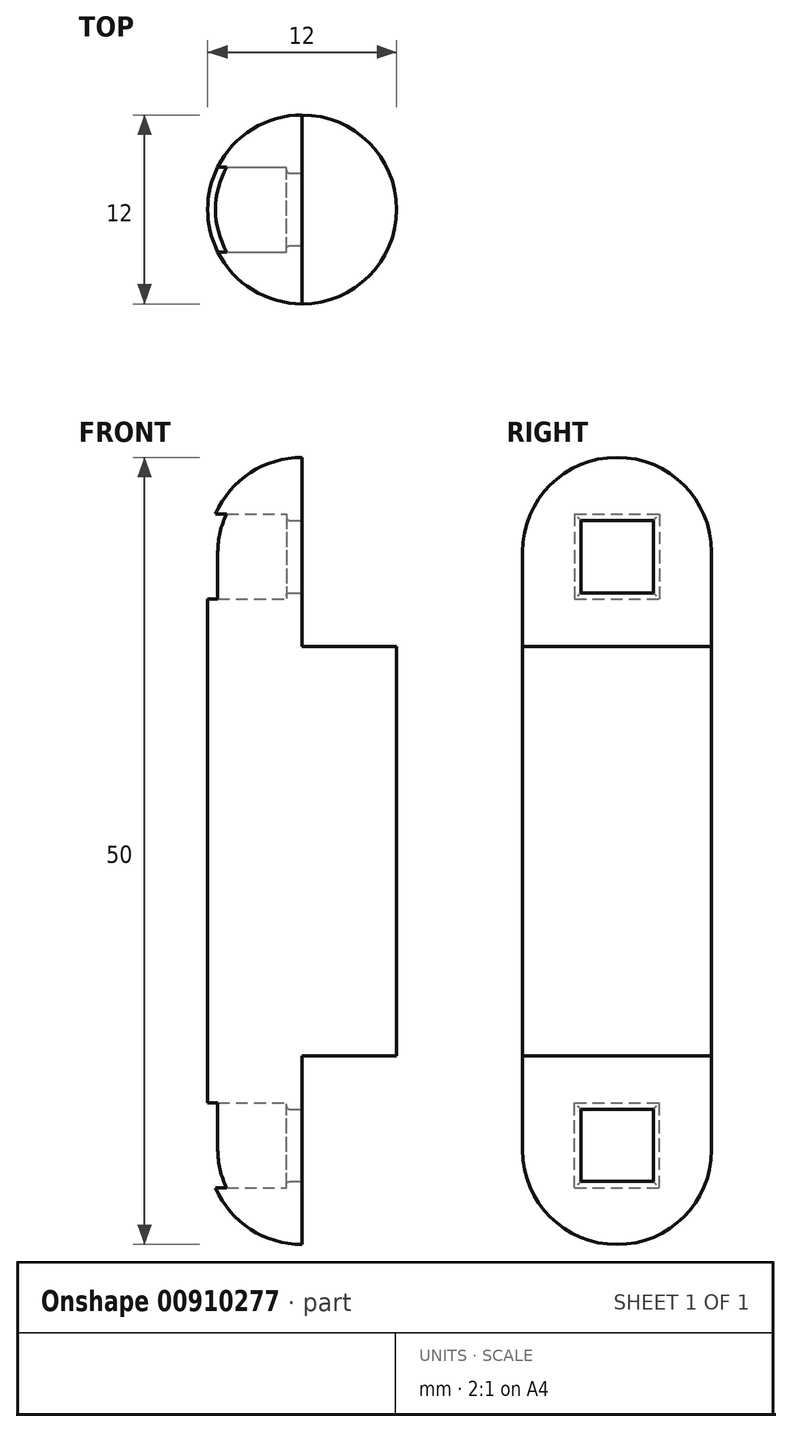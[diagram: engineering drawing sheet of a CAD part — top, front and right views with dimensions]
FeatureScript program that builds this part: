
annotation { "Feature Type Name" : "Feature", "Feature Type Description" : "" }
export const myFeature = defineFeature(function(context is Context, id is Id, definition is map)
    precondition{}
    {
        {
            var Q0;
            Q0=qCreatedBy(makeId("Top.planeOp"),FACE);
            var sketch = newSketch(context, id + "F0", { "sketchPlane" : qUnion([Q0])});
            skCircle(sketch, "E0", {"center": v(0, 0) * mm, "radius": 6 * mm});
            skSolve(sketch);
        }
        {
            var Q0;
            Q0=makeQuery(id+"F0.imprint","IMPRINT",FACE,{"disambiguationData":[TD([[makeQuery(id+"F0.imprint","IMPRINT",EDGE,{"derivedFrom":sQuery(id+"F0.wireOp",EDGE,"E0")}),1.0]])]});
            extrude(context, id + "F1", {"entities" : qUnion([Q0]), "depth" : 25 * mm, "offsetDistance" : 25 * mm});
        }
        {
            var Q0;
            Q0=makeQuery(id+"F1.opExtrude","CAP_EDGE",EDGE,{"disambiguationData":[OSD([sQuery(id+"F0.wireOp",EDGE,"E0")])],"isStart":false});
            fillet(context, id + "F2", {"entities" : qUnion([Q0]), "radius" : 6 * mm, "tangentPropagation" : true, "allowEdgeOverflow" : false});
        }
        {
            var Q0;
            Q0=qCreatedBy(makeId("Front.planeOp"),FACE);
            var sketch = newSketch(context, id + "F3", { "sketchPlane" : qUnion([Q0])});
            skLineSegment(sketch, "E1.bottom", {"start": v(0, 26.9) * mm, "end": v(7.45, 26.9) * mm});
            skLineSegment(sketch, "E1.top", {"start": v(0, 13) * mm, "end": v(7.45, 13) * mm});
            skLineSegment(sketch, "E1.left", {"start": v(0, 26.9) * mm, "end": v(0, 13) * mm});
            skLineSegment(sketch, "E1.right", {"start": v(7.45, 26.9) * mm, "end": v(7.45, 13) * mm});
            skSolve(sketch);
        }
        {
            var Q0;
            Q0=makeQuery(id+"F3.imprint","IMPRINT",FACE,{"disambiguationData":[TD([[makeQuery(id+"F3.imprint","IMPRINT",EDGE,{"derivedFrom":sQuery(id+"F3.wireOp",EDGE,"E1.bottom")}),-1.0]])]});
            extrude(context, id + "F4", {"entities" : qUnion([Q0]), "operationType" : NewBodyOperationType.REMOVE, "endBound" : BoundingType.SYMMETRIC, "depth" : 25 * mm, "offsetDistance" : 25 * mm});
        }
        {
            var Q0;
            Q0=makeQuery(id+"F4.boolean.opBoolean","COPY",FACE,{"derivedFrom":makeQuery(id+"F4.opExtrude","SWEPT_FACE",FACE,{"disambiguationData":[OSD([sQuery(id+"F3.wireOp",EDGE,"E1.left")])]})});
            var sketch = newSketch(context, id + "F5", { "sketchPlane" : qUnion([Q0])});
            skLineSegment(sketch, "E2.bottom", {"start": v(-2.7, 21.4) * mm, "end": v(2.7, 21.4) * mm});
            skLineSegment(sketch, "E2.top", {"start": v(-2.7, 16) * mm, "end": v(2.7, 16) * mm});
            skLineSegment(sketch, "E2.left", {"start": v(-2.7, 21.4) * mm, "end": v(-2.7, 16) * mm});
            skLineSegment(sketch, "E2.right", {"start": v(2.7, 21.4) * mm, "end": v(2.7, 16) * mm});
            skSolve(sketch);
        }
        {
            var Q0;
            Q0=makeQuery(id+"F5.imprint","IMPRINT",FACE,{"disambiguationData":[TD([[makeQuery(id+"F5.imprint","IMPRINT",EDGE,{"derivedFrom":sQuery(id+"F5.wireOp",EDGE,"E2.bottom")}),-1.0]])]});
            extrude(context, id + "F6", {"entities" : qUnion([Q0]), "operationType" : NewBodyOperationType.REMOVE, "oppositeDirection" : true, "depth" : 25 * mm, "offsetDistance" : 25 * mm});
        }
        {
            var Q0;
            Q0=makeQuery(id+"F4.boolean.opBoolean","COPY",FACE,{"derivedFrom":makeQuery(id+"F4.opExtrude","SWEPT_FACE",FACE,{"disambiguationData":[OSD([sQuery(id+"F3.wireOp",EDGE,"E1.left")])]})});
            var sketch = newSketch(context, id + "F7", { "sketchPlane" : qUnion([Q0])});
            skLineSegment(sketch, "E3.bottom", {"start": v(-2.3, 21) * mm, "end": v(2.3, 21) * mm});
            skLineSegment(sketch, "E3.top", {"start": v(-2.3, 16.4) * mm, "end": v(2.3, 16.4) * mm});
            skLineSegment(sketch, "E3.left", {"start": v(-2.3, 21) * mm, "end": v(-2.3, 16.4) * mm});
            skLineSegment(sketch, "E3.right", {"start": v(2.3, 21) * mm, "end": v(2.3, 16.4) * mm});
            skLineSegment(sketch, "E4.bottom", {"start": v(-3.32, 22.07) * mm, "end": v(3.51, 22.07) * mm});
            skLineSegment(sketch, "E4.top", {"start": v(-3.32, 15.48) * mm, "end": v(3.51, 15.48) * mm});
            skLineSegment(sketch, "E4.left", {"start": v(-3.32, 22.07) * mm, "end": v(-3.32, 15.48) * mm});
            skLineSegment(sketch, "E4.right", {"start": v(3.51, 22.07) * mm, "end": v(3.51, 15.48) * mm});
            skSolve(sketch);
        }
        {
            var Q0;
            Q0=makeQuery(id+"F7.imprint","IMPRINT",FACE,{"disambiguationData":[TD([[makeQuery(id+"F7.imprint","IMPRINT",EDGE,{"derivedFrom":sQuery(id+"F7.wireOp",EDGE,"E3.bottom")}),1.0]])]});
            extrude(context, id + "F8", {"entities" : qUnion([Q0]), "operationType" : NewBodyOperationType.ADD, "oppositeDirection" : true, "depth" : 1 * mm, "offsetDistance" : 25 * mm});
        }
        {
            var Q0;
            Q0=makeQuery(id+"F8.opExtrude","CAP_EDGE",EDGE,{"disambiguationData":[OSD([sQuery(id+"F7.wireOp",EDGE,"E3.top")])],"isStart":false});
            var Q1;
            Q1=makeQuery(id+"F8.opExtrude","CAP_EDGE",EDGE,{"disambiguationData":[OSD([sQuery(id+"F7.wireOp",EDGE,"E3.right")])],"isStart":false});
            var Q2;
            Q2=makeQuery(id+"F8.opExtrude","CAP_EDGE",EDGE,{"disambiguationData":[OSD([sQuery(id+"F7.wireOp",EDGE,"E3.bottom")])],"isStart":false});
            var Q3;
            Q3=makeQuery(id+"F8.opExtrude","CAP_EDGE",EDGE,{"disambiguationData":[OSD([sQuery(id+"F7.wireOp",EDGE,"E3.left")])],"isStart":false});
            var Q4;
            Q4=makeQuery(id+"F8.opExtrude","CAP_EDGE",EDGE,{"disambiguationData":[OSD([sQuery(id+"F5.wireOp",EDGE,"E2.bottom")])],"isStart":false});
            var Q5;
            Q5=makeQuery(id+"F8.opExtrude","CAP_EDGE",EDGE,{"disambiguationData":[OSD([sQuery(id+"F5.wireOp",EDGE,"E2.left")])],"isStart":false});
            var Q6;
            Q6=makeQuery(id+"F8.opExtrude","CAP_EDGE",EDGE,{"disambiguationData":[OSD([sQuery(id+"F5.wireOp",EDGE,"E2.right")])],"isStart":false});
            var Q7;
            Q7=makeQuery(id+"F8.opExtrude","CAP_EDGE",EDGE,{"disambiguationData":[OSD([sQuery(id+"F5.wireOp",EDGE,"E2.top")])],"isStart":false});
            fillet(context, id + "F9", {"entities" : qUnion([Q0, Q1, Q2, Q3, Q4, Q5, Q6, Q7]), "radius" : 0.2 * mm, "tangentPropagation" : true, "allowEdgeOverflow" : false});
        }
        {
            var Q0;
            Q0=makeQuery(id+"F1.opExtrude","SWEPT_BODY",BODY,{"disambiguationData":[OSD([sQuery(id+"F0.wireOp",EDGE,"E0")])]});
            var Q1;
            Q1=qCreatedBy(makeId("Top.planeOp"),FACE);
            mirror(context, id + "F10", {"operationType" : NewBodyOperationType.ADD, "entities" : qUnion([Q0]), "mirrorPlane" : qUnion([Q1])});
        }
    });
